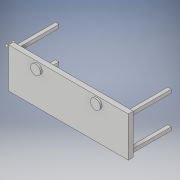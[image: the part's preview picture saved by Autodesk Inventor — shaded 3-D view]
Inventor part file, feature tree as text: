
AUTODESK INVENTOR PART (.ipt)
format: ipt  version: 2019 (Build 230136000, 136)  size: 146,944 bytes
history: native  units: mm
features: extrude x5, sketch x4
ambient origin geometry x8: Origin, YZ Plane, XZ Plane, XY Plane, X Axis, Y Axis, Z Axis, Center Point
bodies: Solid1 (feature_tree)
feature tree (9):
  sketch  "Sketch1"  dims[d0=2400.0mm d1=800.0mm]
  extrude  "Extrusion1"  Depth=800.0mm
  extrude  "Extrusion2"  Depth=125.0mm
  sketch  "Sketch2"  dims[d2=575.0mm d3=125.0mm]
  extrude  "Extrusion3"  Depth=200.0mm
  extrude  "Extrusion4"  Depth=100.0mm TaperAngle=0.0deg
  sketch  "Sketch3"  dims[d4=1775.0mm d5=200.0mm]
  extrude  "Extrusion5"  Depth=100.0mm TaperAngle=0.0deg
  sketch  "Sketch4"  dims[d6=35.0mm d7=0.0mm d8=100.0mm d9=0.0mm d10=100.0mm d11=0.0mm d12=100.0mm d13=0.0mm d14=40.0mm d15=40.0mm d16=70.0mm d17=70.0mm d18=40.0mm d19=40.0mm d20=70.0mm d21=70.0mm d22=40.0mm d23=40.0mm d24=70.0mm d25=70.0mm d26=70.0mm d27=70.0mm d28=800.0mm d29=0.0mm]
